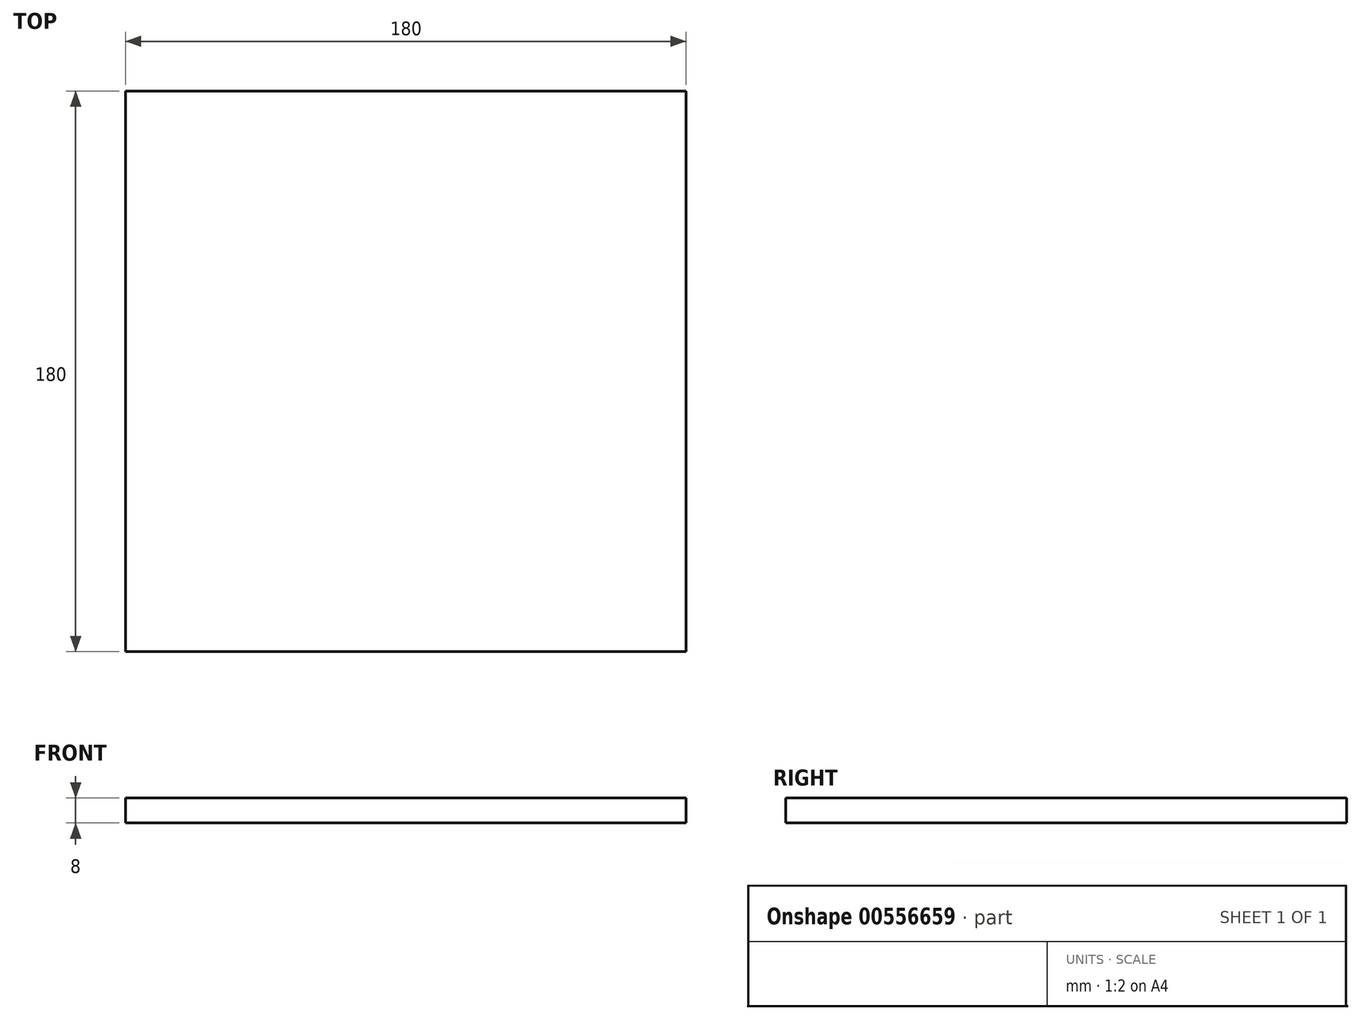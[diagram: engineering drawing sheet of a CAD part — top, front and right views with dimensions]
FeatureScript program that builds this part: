
annotation { "Feature Type Name" : "Feature", "Feature Type Description" : "" }
export const myFeature = defineFeature(function(context is Context, id is Id, definition is map)
    precondition{}
    {
        {
            var Q0;
            Q0=qCreatedBy(makeId("Top.planeOp"),FACE);
            var sketch = newSketch(context, id + "F0", { "sketchPlane" : qUnion([Q0])});
            skLineSegment(sketch, "E0", {"start": v(0, 0) * mm, "end": v(0, 180) * mm});
            skLineSegment(sketch, "E1", {"start": v(0, 180) * mm, "end": v(180, 180) * mm});
            skLineSegment(sketch, "E2", {"start": v(180, 180) * mm, "end": v(180, 0) * mm});
            skLineSegment(sketch, "E3", {"start": v(180, 0) * mm, "end": v(0, 0) * mm});
            skSolve(sketch);
        }
        {
            var Q0;
            Q0=makeQuery(id+"F0.imprint","IMPRINT",FACE,{"disambiguationData":[TD([[makeQuery(id+"F0.imprint","IMPRINT",EDGE,{"derivedFrom":sQuery(id+"F0.wireOp",EDGE,"E0")}),-1.0]])]});
            extrude(context, id + "F1", {"entities" : qUnion([Q0]), "depth" : 8 * mm, "offsetDistance" : 25 * mm});
        }
    });
